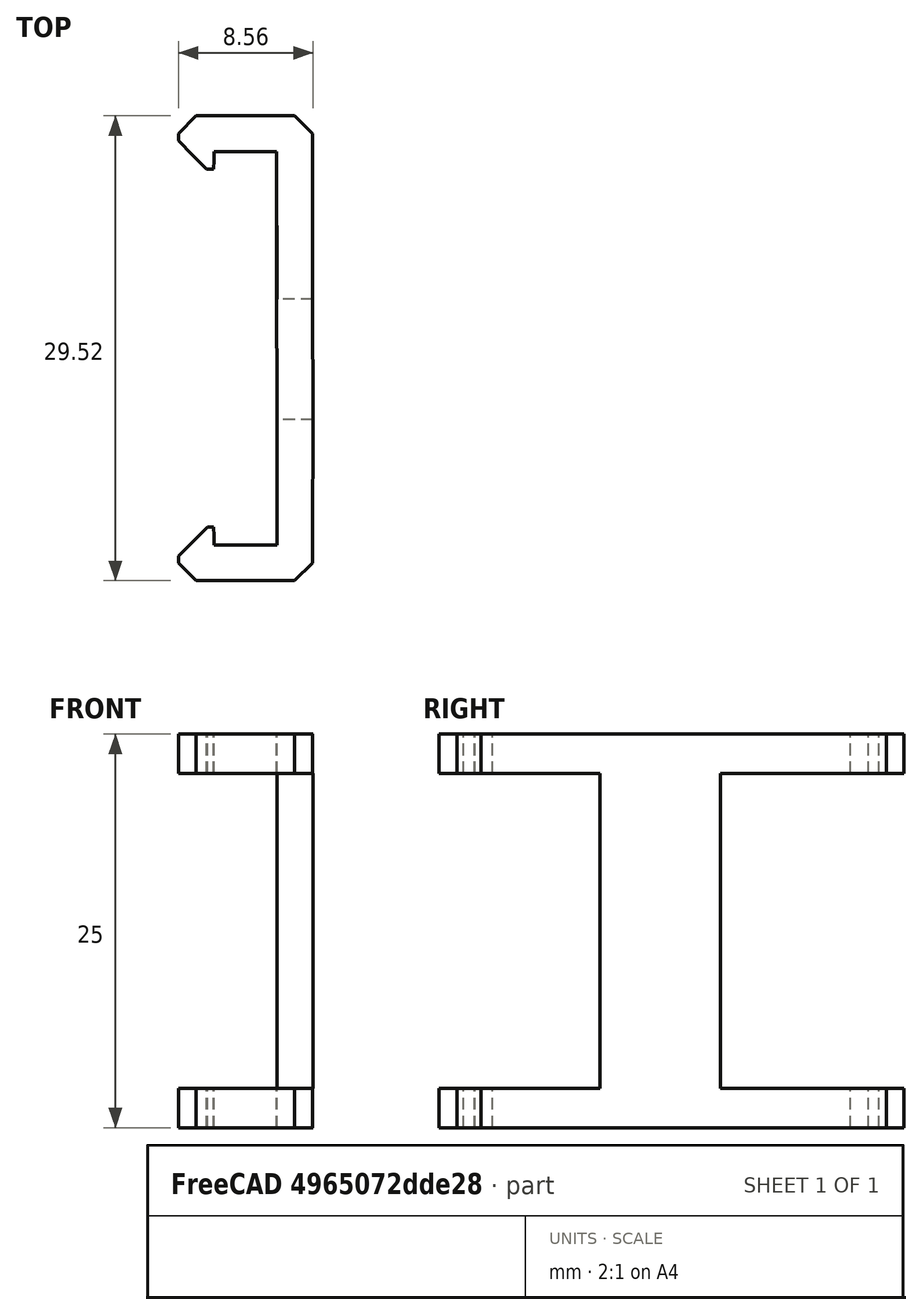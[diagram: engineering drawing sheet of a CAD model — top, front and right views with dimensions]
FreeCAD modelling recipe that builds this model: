
FCSTD DOCUMENT  (FreeCAD 1.0R39109 (Git))
Label: KameraHalterung-DerGerät1
License: All rights reserved
LicenseURL: https://en.wikipedia.org/wiki/All_rights_reserved
objects: Sketcher::SketchObject×2, PartDesign::Pad×1, PartDesign::Pocket×1, PartDesign::Body×1
note: 11 computed .brp shape members not serialized (recipe doc carries the construction recipe); baked Part::Feature solids carry a one-line shape summary decoded from their .brp

FEATURE [Sketcher::SketchObject] Sketch
  ArcFitTolerance = 1e-06
  FullyConstrained = false
  MakeInternals = false
  sketch-geometry (40):
    g0: LineSegment StartX=9.69333 StartY=3.30899 StartZ=0 EndX=9.6822 EndY=1.77559 EndZ=0
    g1: LineSegment StartX=9.6822 StartY=1.77559 StartZ=0 EndX=9.12216 EndY=1.21439 EndZ=0
    g2: LineSegment StartX=9.12216 StartY=1.21439 StartZ=0 EndX=8.56212 EndY=0.653199 EndZ=0
    g3: LineSegment StartX=8.56212 StartY=0.653199 StartZ=0 EndX=5.42803 EndY=0.653199 EndZ=0
    g4: LineSegment StartX=2.29394 StartY=0.653199 StartZ=0 EndX=1.73221 EndY=1.21378 EndZ=0
    g5: LineSegment StartX=5.42803 StartY=0.653199 StartZ=0 EndX=2.29394 EndY=0.653199 EndZ=0
    g6: LineSegment StartX=1.73221 StartY=1.21378 StartZ=0 EndX=1.17047 EndY=1.77436 EndZ=0
    g7: LineSegment StartX=1.17047 StartY=1.77436 StartZ=0 EndX=1.17048 EndY=1.98706 EndZ=0
    g8: LineSegment StartX=1.17048 StartY=1.98706 StartZ=0 EndX=1.17048 EndY=2.19978 EndZ=0
    g9: LineSegment StartX=2.092 StartY=3.12058 StartZ=0 EndX=3.01351 EndY=4.04138 EndZ=0
    g10: LineSegment StartX=1.17048 StartY=2.19978 StartZ=0 EndX=2.092 EndY=3.12058 EndZ=0
    g11: LineSegment StartX=3.01351 StartY=4.04138 StartZ=0 EndX=3.21309 EndY=4.04137 EndZ=0
    g12: LineSegment StartX=3.21309 StartY=4.04137 StartZ=0 EndX=3.41268 EndY=4.04137 EndZ=0
    g13: LineSegment StartX=3.41268 StartY=4.04137 StartZ=0 EndX=3.4245 EndY=3.4802 EndZ=0
    g14: LineSegment StartX=3.4245 StartY=3.4802 StartZ=0 EndX=3.43632 EndY=2.91903 EndZ=0
    g15: LineSegment StartX=3.43632 StartY=2.91903 StartZ=0 EndX=5.43652 EndY=2.90804 EndZ=0
    g16: LineSegment StartX=5.43652 StartY=2.90804 StartZ=0 EndX=7.43673 EndY=2.89704 EndZ=0
    g17: LineSegment StartX=7.43673 StartY=2.89704 StartZ=0 EndX=7.42708 EndY=15.402 EndZ=0
    g18: LineSegment StartX=7.42708 StartY=15.402 StartZ=0 EndX=7.41744 EndY=27.9069 EndZ=0
    g19: LineSegment StartX=7.41744 StartY=27.9069 StartZ=0 EndX=5.42688 EndY=27.9069 EndZ=0
    g20: LineSegment StartX=3.42451 StartY=27.3457 StartZ=0 EndX=3.41269 EndY=26.7846 EndZ=0
    g21: LineSegment StartX=3.43633 StartY=27.9069 StartZ=0 EndX=3.42451 EndY=27.3457 EndZ=0
    g22: LineSegment StartX=5.42688 StartY=27.9069 StartZ=0 EndX=3.43633 EndY=27.9069 EndZ=0
    g23: LineSegment StartX=3.41269 StartY=26.7846 StartZ=0 EndX=3.19119 EndY=26.7845 EndZ=0
    g24: LineSegment StartX=3.19119 StartY=26.7845 StartZ=0 EndX=2.9697 EndY=26.7845 EndZ=0
    g25: LineSegment StartX=2.9697 StartY=26.7845 StartZ=0 EndX=2.0701 EndY=27.6849 EndZ=0
    g26: LineSegment StartX=2.0701 StartY=27.6849 StartZ=0 EndX=1.17048 EndY=28.5853 EndZ=0
    g27: LineSegment StartX=1.17048 StartY=28.5853 StartZ=0 EndX=1.17048 EndY=28.8172 EndZ=0
    g28: LineSegment StartX=1.17048 StartY=28.8172 StartZ=0 EndX=1.17048 EndY=29.0492 EndZ=0
    g29: LineSegment StartX=1.17048 StartY=29.0492 StartZ=0 EndX=1.73106 EndY=29.6109 EndZ=0
    g30: LineSegment StartX=2.29164 StartY=30.1727 StartZ=0 EndX=5.42688 EndY=30.1727 EndZ=0
    g31: LineSegment StartX=1.73106 StartY=29.6109 StartZ=0 EndX=2.29164 EndY=30.1727 EndZ=0
    g32: LineSegment StartX=5.42688 StartY=30.1727 StartZ=0 EndX=8.56212 EndY=30.1727 EndZ=0
    g33: LineSegment StartX=8.56212 StartY=30.1727 StartZ=0 EndX=9.12253 EndY=29.6112 EndZ=0
    g34: LineSegment StartX=9.12253 StartY=29.6112 StartZ=0 EndX=9.68294 EndY=29.0496 EndZ=0
    g35: LineSegment StartX=9.68294 StartY=29.0496 StartZ=0 EndX=9.6937 EndY=23.785 EndZ=0
    g36: LineSegment StartX=9.6937 StartY=23.785 StartZ=0 EndX=9.70445 EndY=18.5203 EndZ=0
    g37: LineSegment StartX=9.70445 StartY=18.5203 StartZ=0 EndX=9.72654 EndY=10.8666 EndZ=0
    g38: LineSegment StartX=9.72654 StartY=10.8666 StartZ=0 EndX=9.69332 EndY=3.309 EndZ=0
    g39: LineSegment StartX=9.69332 StartY=3.309 StartZ=0 EndX=9.69333 EndY=3.30899 EndZ=0
FEATURE [PartDesign::Pad] Pad
  Direction = (0,0,1)
  Length = 25
  Length2 = 10
  Profile = -> Sketch
  ReferenceAxis = -> Sketch [N_Axis]
  Refine = true
  Suppressed = false
  Type = 0
FEATURE [Sketcher::SketchObject] Sketch001
  ArcFitTolerance = 1e-06
  AttachmentSupport = -> [Pad]
  ExternalGeometry = -> [Pad]
  FullyConstrained = true
  MakeInternals = false
  MapMode = 5
  Placement = pos=(9.67859,-0.0425364,0) rot=(0.579042,0.576503,0.576503;2.09186rad)
  sketch-geometry (8):
    g0: LineSegment StartX=10.9092 StartY=2.5 StartZ=0 EndX=10.9092 EndY=22.5 EndZ=0
    g1: LineSegment StartX=10.9092 StartY=22.5 StartZ=0 EndX=-0.090765 EndY=22.5 EndZ=0
    g2: LineSegment StartX=-0.090765 StartY=22.5 StartZ=0 EndX=-0.090765 EndY=2.5 EndZ=0
    g3: LineSegment StartX=-0.090765 StartY=2.5 StartZ=0 EndX=10.9092 EndY=2.5 EndZ=0
    g4: LineSegment StartX=18.5628 StartY=2.5 StartZ=0 EndX=30.5628 EndY=2.5 EndZ=0
    g5: LineSegment StartX=30.5628 StartY=2.5 StartZ=0 EndX=30.5628 EndY=22.5 EndZ=0
    g6: LineSegment StartX=30.5628 StartY=22.5 StartZ=0 EndX=18.5628 EndY=22.5 EndZ=0
    g7: LineSegment StartX=18.5628 StartY=22.5 StartZ=0 EndX=18.5628 EndY=2.5 EndZ=0
  constraints (20):
    c: Coincident(g0,g1)
    c: Coincident(g1,g2)
    c: Coincident(g2,g3)
    c: Coincident(g3,g0)
    c: Vertical(g2)
    c: Horizontal(g1)
    c: Horizontal(g3)
    c: Coincident(g4,g5)
    c: Coincident(g5,g6)
    c: Coincident(g6,g7)
    c: Coincident(g7,g4)
    c: Vertical(g5)
    c: Tangent(g4,g3)
    c: Tangent(g1,g6)
    c: Tangent(g-3,g7)
    c: Tangent(g-4,g0)
    c: DistanceX(g3,g3) = 11
    c: DistanceX(g4,g4) = 12
    c: DistanceY(g5,g5) = 20
    c: DistanceY(g-1,g4) = 2.5
FEATURE [PartDesign::Pocket] Pocket
  BaseFeature = -> Pad
  Direction = (-0.99999,0.00439485,0)
  Length = 5
  Length2 = 5
  Profile = -> Sketch001
  ReferenceAxis = -> Sketch001 [N_Axis]
  Refine = true
  Suppressed = false
  Type = 1
FEATURE [PartDesign::Body] Body
  AllowCompound = false
  Group = -> [Sketch,Pad,Sketch001,Pocket]
  Origin = -> Origin
  Tip = -> Pocket
